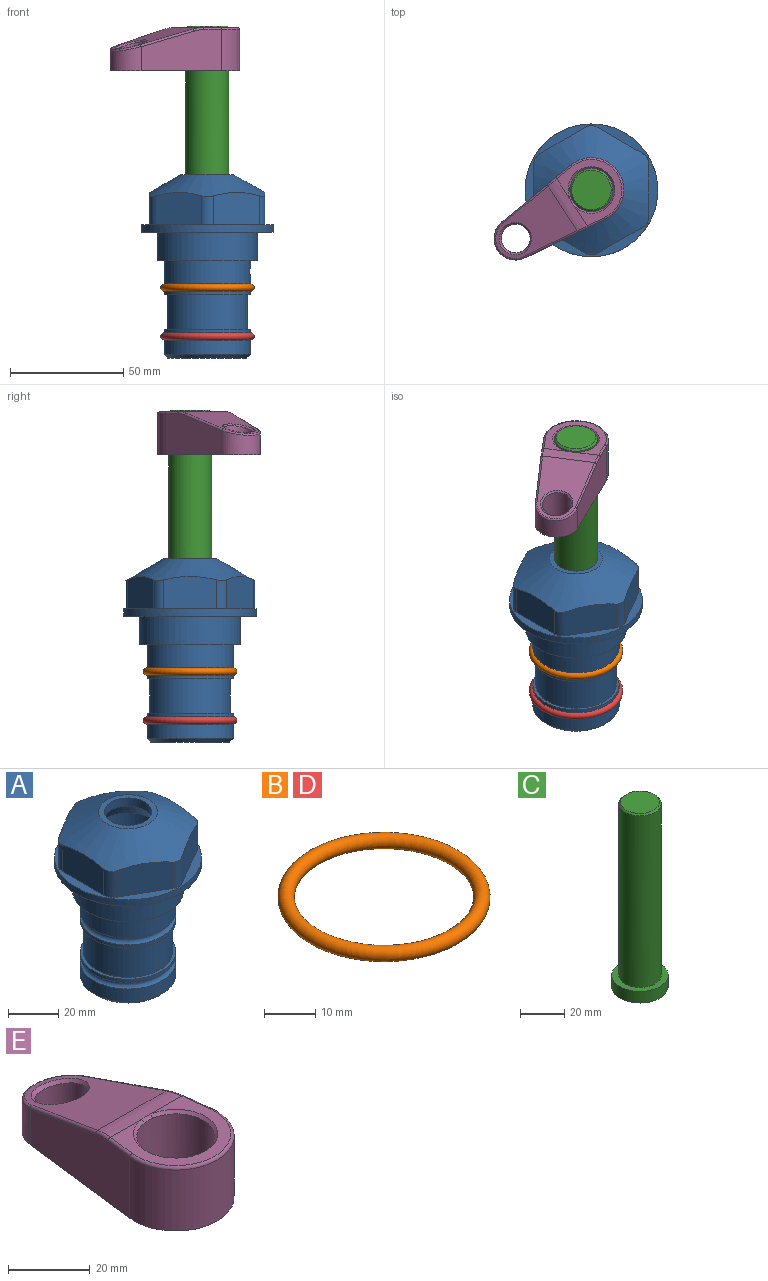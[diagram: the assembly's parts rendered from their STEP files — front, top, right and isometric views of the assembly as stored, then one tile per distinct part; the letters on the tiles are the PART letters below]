
ASSEMBLY  parts=5 mates=4
PART A: 36 faces, bbox 58.7x58.7x81 mm
  f0: cylinder r=17.78mm len=35.56mm, axis (0,0,1), area 1670.8mm2, adj f23,f24,f31
  f1: cylinder r=19.05mm len=38.1mm, axis (0,0,1), area 1191.9mm2, adj f26,f27,f30
  f2: plane 58.66x58.66mm, normal (0,0,-1), area 1150.6mm2, adj f3,f28
  f3: cylinder r=29.33mm len=58.66mm, axis (0,0,-1), area 585.1mm2, adj f2,f4
  f4: plane 58.66x58.66mm, normal (0,0,1), area 475.9mm2, adj f3,f5,f6,f7,f8,f9,f10,f11
  f5: plane 20.32x14.34mm, normal (-0.5,0.87,0), area 324.4mm2, adj f4,f15,f16,f17
  f6: plane 20.32x14.34mm, normal (0.5,0.87,0), area 324.4mm2, adj f4,f14,f15,f17
  f7: plane 23.48x14.34mm, normal (1,0,0), area 324.4mm2, adj f4,f13,f14,f17
  f8: plane 20.32x14.34mm, normal (0.5,-0.87,0), area 324.4mm2, adj f4,f12,f13,f17
  f9: plane 20.32x14.34mm, normal (-0.5,-0.87,0), area 324.4mm2, adj f4,f11,f12,f17
  f10: plane 23.48x14.34mm, normal (-1,0,0), area 324.4mm2, adj f4,f11,f16,f17
  f11: cylinder r=5.08mm len=12.85mm, axis (0,0,-1), area 67.2mm2, adj f4,f9,f10,f17
  f12: cylinder r=5.08mm len=12.85mm, axis (0,0,-1), area 67.2mm2, adj f4,f8,f9,f17
  f13: cylinder r=5.08mm len=12.85mm, axis (0,0,-1), area 67.2mm2, adj f4,f7,f8,f17
  f14: cylinder r=5.08mm len=12.85mm, axis (0,0,-1), area 67.2mm2, adj f4,f6,f7,f17
  f15: cylinder r=5.08mm len=12.85mm, axis (0,0,-1), area 67.2mm2, adj f4,f5,f6,f17
  f16: cylinder r=5.08mm len=12.85mm, axis (0,0,-1), area 67.2mm2, adj f4,f5,f10,f17
  f17: cone r=11.73mm half-angle=60deg, axis (0,0,-1), area 2071.8mm2, adj f5,f6,f7,f8,f9,f10,f11,f12
  f18: plane 23.46x23.46mm, normal (0,0,1), area 147.4mm2, adj f17,f35
  f19: plane 34.93x34.93mm, normal (0,0,-1), area 958mm2, adj f29
  f20: cylinder r=19.05mm len=38.1mm, axis (0,0,1), area 760.1mm2, adj f21,f29
  f21: torus R=19.05mm, axis (0,0,1), area 565.3mm2, adj f20,f22
  f22: cylinder r=19.05mm len=38.1mm, axis (0,0,1), area 190mm2, adj f21,f23
  f23: plane 38.1x38.1mm, normal (0,0,1), area 146.9mm2, adj f0,f22
  f24: plane 38.1x38.1mm, normal (0,0,-1), area 146.9mm2, adj f0,f25
  f25: cylinder r=19.05mm len=38.1mm, axis (0,0,1), area 190mm2, adj f24,f26
  f26: torus R=19.05mm, axis (0,0,1), area 565.3mm2, adj f1,f25
  f27: plane 44.45x44.45mm, normal (0,0,-1), area 411.7mm2, adj f1,f28
  f28: cylinder r=22.23mm len=44.45mm, axis (0,0,1), area 1773.5mm2, adj f2,f27
  f29: cone r=19.05mm half-angle=45deg, axis (0,0,1), area 257.5mm2, adj f19,f20
  f30: cylinder r=3.17mm len=6.75mm, axis (-1,0,0), area 128mm2, adj f1,f33
  f31: cylinder r=3.17mm len=6.35mm, axis (-1,0,0), area 102.5mm2, adj f0,f33
  f32: plane 25.4x25.4mm, normal (0,0,1), area 506.7mm2, adj f33
  f33: cylinder r=12.7mm len=66.42mm, axis (0,0,-1), area 5236.2mm2, adj f30,f31,f32,f34
  f34: cone r=9.53mm half-angle=30deg, axis (0,0,-1), area 443.4mm2, adj f33,f35
  f35: cylinder r=9.53mm len=19.05mm, axis (0,0,-1), area 240.9mm2, adj f18,f34
PART B: 1 faces, bbox 44.7x44.7x3.2 mm
  f0: torus R=19.05mm, axis (0,0,1), area 1193.9mm2
PART C: 6 faces, bbox 25.4x25.4x101.6 mm
  f0: plane 17.46x17.46mm, normal (0,0,1), area 239.5mm2, adj f5
  f1: plane 25.4x25.4mm, normal (0,0,-1), area 506.7mm2, adj f2
  f2: cylinder r=12.7mm len=25.4mm, axis (0,0,1), area 506.7mm2, adj f1,f3
  f3: plane 25.4x25.4mm, normal (0,0,1), area 221.7mm2, adj f2,f4
  f4: cylinder r=9.53mm len=94.46mm, axis (0,0,1), area 5653mm2, adj f3,f5
  f5: cone r=8.73mm half-angle=45deg, axis (0,0,-1), area 64.4mm2, adj f0,f4
PART D: same geometry as B
PART E: 31 faces, bbox 31.7x65.5x19.8 mm
  f0: plane 39.12x18.26mm, normal (0.99,0.12,0), area 612.2mm2, adj f1,f4,f7,f11,f13,f15
  f1: cylinder r=9.53mm len=18.91mm, axis (0,0,-1), area 296.1mm2, adj f0,f2,f7,f17
  f2: plane 39.12x18.26mm, normal (-0.99,0.12,0), area 612.2mm2, adj f1,f4,f7,f12,f14,f16
  f3: cylinder r=6.35mm len=12.7mm, axis (0,0,-1), area 362.4mm2, adj f7,f18
  f4: cylinder r=14.29mm len=28.58mm, axis (0,0,-1), area 882.2mm2, adj f0,f2,f7,f10
  f5: cylinder r=9.53mm len=19.05mm, axis (0,0,-1), area 1092.6mm2, adj f7,f19,f20
  f6: plane 26.99x23.69mm, normal (0,0,1), area 216.2mm2, adj f9,f10,f11,f12,f19
  f7: plane 63.5x28.58mm, normal (0,0,-1), area 661.8mm2, adj f0,f1,f2,f3,f4,f5,f22,f23
  f8: plane 33.52x23.6mm, normal (0,0.26,0.97), area 486mm2, adj f9,f15,f16,f17,f18
  f9: cylinder r=19.05mm len=24.72mm, axis (1,0,0), area 120.4mm2, adj f6,f8,f13,f14,f20
  f10: torus R=13.49mm, axis (0,0,1), area 59mm2, adj f4,f6,f11,f12
  f11: cylinder r=0.79mm len=8.67mm, axis (0.12,-0.99,0), area 10.8mm2, adj f0,f6,f10,f13
  f12: cylinder r=0.79mm len=8.67mm, axis (0.12,0.99,0), area 10.8mm2, adj f2,f6,f10,f14
  f13: bspline ~4.95x1.42mm, area 6.1mm2, adj f0,f9,f11,f15
  f14: bspline ~4.95x1.42mm, area 6.1mm2, adj f2,f9,f12,f16
  f15: cylinder r=0.79mm len=25.95mm, axis (0.12,-0.96,0.26), area 32.9mm2, adj f0,f8,f13,f17
  f16: cylinder r=0.79mm len=25.95mm, axis (0.12,0.96,-0.26), area 32.9mm2, adj f2,f8,f14,f17
  f17: bspline ~18.91x8.38mm, area 30mm2, adj f1,f8,f15,f16
  f18: bspline ~14.29x14.29mm, area 48.3mm2, adj f3,f8
  f19: cone r=9.53mm half-angle=45deg, axis (0,0,1), area 66.5mm2, adj f5,f6,f20
  f20: bspline ~3.22x0.96mm, area 3.5mm2, adj f5,f9,f19
  f21: plane 2.75x2.72mm, normal (0,0,-1), area 2.9mm2, adj f23,f25,f28
  f22: plane 23.05x15.88mm, normal (-0.99,-0.12,0), area 323.6mm2, adj f7,f25,f26,f27,f28,f29
  f23: plane 23.05x15.88mm, normal (0.99,-0.12,0), area 323.6mm2, adj f7,f21,f25,f27,f28,f30
  f24: cylinder r=9.53mm len=10.69mm, axis (0,0,-1), area 114.7mm2, adj f7,f27,f29,f30
  f25: cylinder r=12.7mm len=20.59mm, axis (0,0,-1), area 381.1mm2, adj f7,f21,f22,f23,f26,f28
  f26: plane 2.75x2.72mm, normal (0,0,-1), area 2.9mm2, adj f22,f25,f28
  f27: plane 19.72x18.37mm, normal (0,-0.26,-0.97), area 291.8mm2, adj f22,f23,f24,f28,f29,f30
  f28: cylinder r=15.88mm len=19.92mm, axis (1,0,0), area 54.8mm2, adj f21,f22,f23,f25,f26,f27
  f29: cylinder r=1.59mm len=11mm, axis (0,0,-1), area 34.7mm2, adj f7,f22,f24,f27
  f30: cylinder r=1.59mm len=11mm, axis (0,0,-1), area 34.7mm2, adj f7,f23,f24,f27
PLACE A at identity fixed
PLACE B at identity
PLACE C rot(axis=(0,0,1),122.6deg) t=(0,0,27.55)mm
PLACE D t=(0,0,-21.59)mm
PLACE E rot(axis=(0,0,1),122.6deg) t=(0,0,26.76)mm
MATE fastened D.f0 <-> A.f0  axis (0,0,1) through (0,0,-46.1)mm
MATE cylindrical C.f2 <-> A.f0  axis (0,0,-1) through (0,0,-10.55)mm
MATE fastened E.f4 <-> C.f2  axis (0,0,1) through (0,0,90.26)mm
MATE fastened B.f0 <-> A.f0  axis (0,0,1) through (0,0,-24.51)mm
